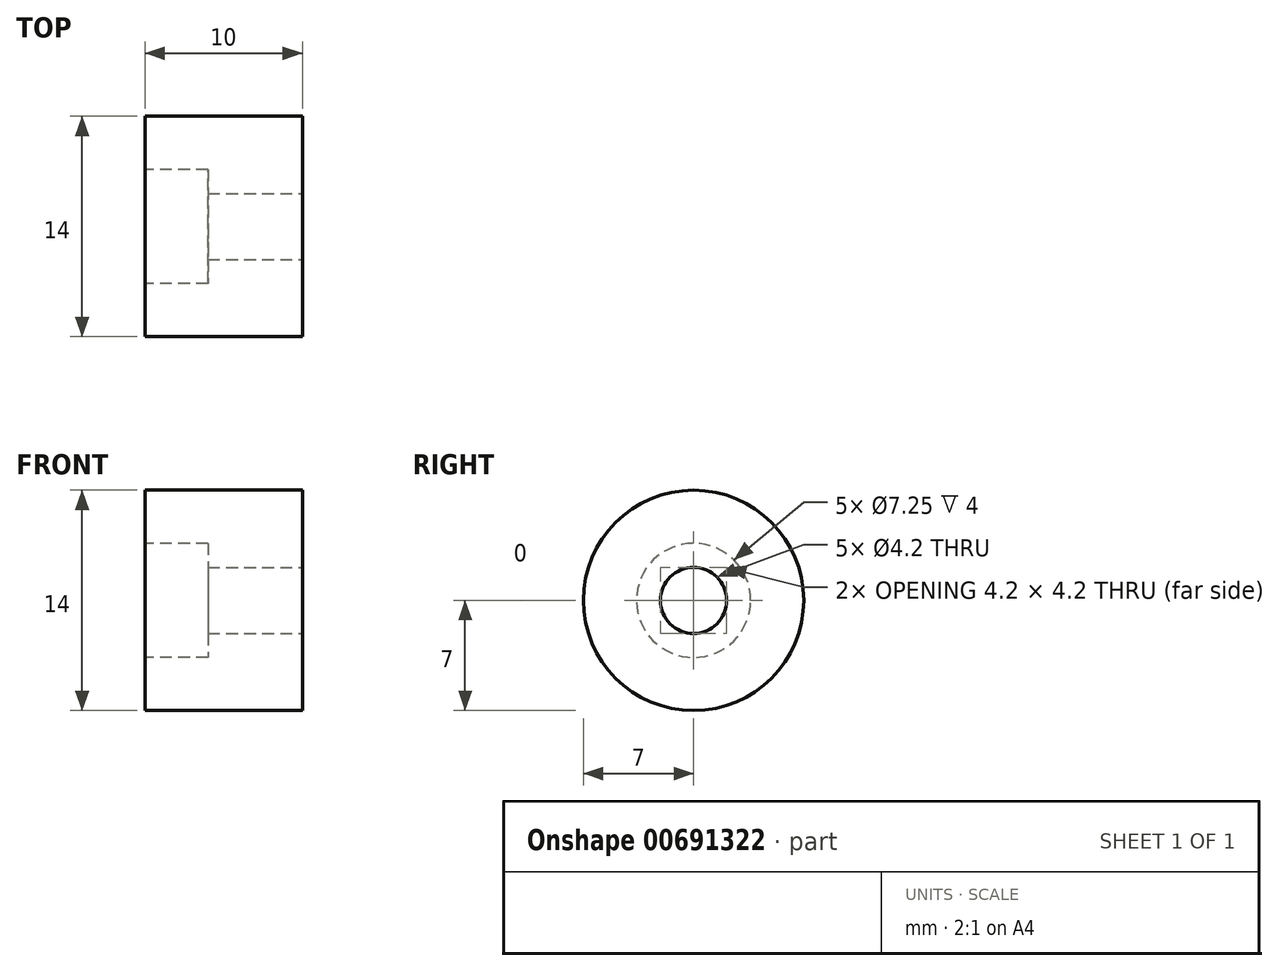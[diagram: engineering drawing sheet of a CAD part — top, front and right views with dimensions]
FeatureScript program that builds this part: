
annotation { "Feature Type Name" : "Feature", "Feature Type Description" : "" }
export const myFeature = defineFeature(function(context is Context, id is Id, definition is map)
    precondition{}
    {
        {
            var Q0;
            Q0=qCreatedBy(makeId("Right.planeOp"),FACE);
            var sketch = newSketch(context, id + "F0", { "sketchPlane" : qUnion([Q0])});
            skCircle(sketch, "E0", {"center": v(0, 0) * mm, "radius": 7 * mm});
            skSolve(sketch);
        }
        {
            var Q0;
            Q0=qSketchRegion(id+"F0",true);
            extrude(context, id + "F1", {"entities" : qUnion([Q0]), "depth" : 10 * mm, "offsetDistance" : 25.4 * mm});
        }
        {
            var Q0;
            Q0=makeQuery(id+"F1.opExtrude","CAP_FACE",FACE,{"disambiguationData":[OSD([sQuery(id+"F0.wireOp",EDGE,"E0")])],"isStart":true});
            var sketch = newSketch(context, id + "F2", { "sketchPlane" : qUnion([Q0])});
            skCircle(sketch, "E1", {"center": v(0, 0) * mm, "radius": 3.62 * mm});
            skSolve(sketch);
        }
        {
            var Q0;
            Q0=makeQuery(id+"F2.imprint","IMPRINT",FACE,{"disambiguationData":[TD([[makeQuery(id+"F2.imprint","IMPRINT",EDGE,{"derivedFrom":sQuery(id+"F2.wireOp",EDGE,"E1")}),1.0]])]});
            var Q1;
            Q1=sQuery(id+"F2.wireOp",EDGE,"E1");
            extrude(context, id + "F3", {"entities" : qUnion([Q0]), "operationType" : NewBodyOperationType.REMOVE, "surfaceEntities" : qUnion([Q1]), "oppositeDirection" : true, "depth" : 4 * mm, "offsetDistance" : 25.4 * mm});
        }
        {
            var Q0;
            Q0=makeQuery(id+"F1.opExtrude","CAP_FACE",FACE,{"disambiguationData":[OSD([sQuery(id+"F0.wireOp",EDGE,"E0")])],"isStart":false});
            var sketch = newSketch(context, id + "F4", { "sketchPlane" : qUnion([Q0])});
            skCircle(sketch, "E2", {"center": v(0, 0) * mm, "radius": 2.1 * mm});
            skSolve(sketch);
        }
        {
            var Q0;
            Q0=makeQuery(id+"F4.imprint","IMPRINT",FACE,{"disambiguationData":[TD([[makeQuery(id+"F4.imprint","IMPRINT",EDGE,{"derivedFrom":sQuery(id+"F4.wireOp",EDGE,"E2")}),1.0]])]});
            extrude(context, id + "F5", {"entities" : qUnion([Q0]), "operationType" : NewBodyOperationType.REMOVE, "endBound" : BoundingType.THROUGH_ALL, "oppositeDirection" : true, "depth" : 25.4 * mm, "offsetDistance" : 25.4 * mm});
        }
    });
